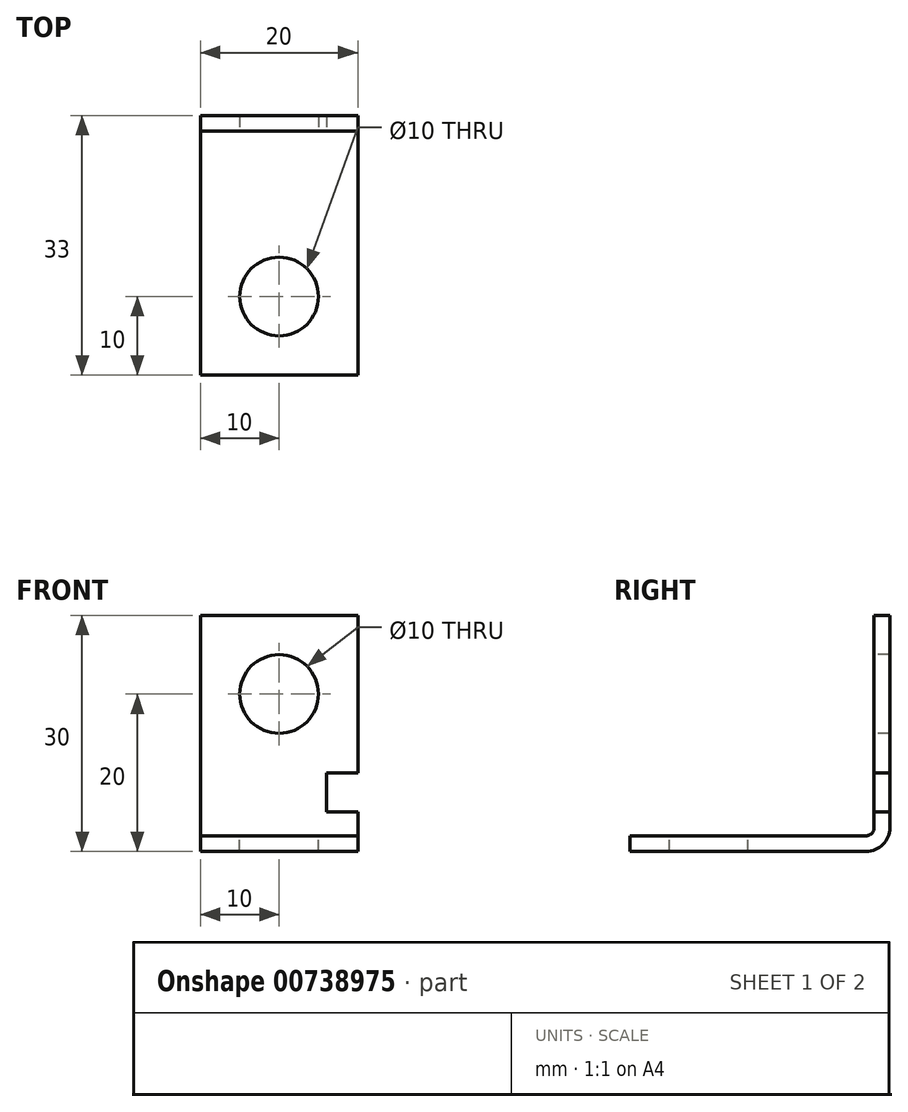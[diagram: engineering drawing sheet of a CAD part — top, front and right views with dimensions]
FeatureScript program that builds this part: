
annotation { "Feature Type Name" : "Feature", "Feature Type Description" : "" }
export const myFeature = defineFeature(function(context is Context, id is Id, definition is map)
    precondition{}
    {
        {
            var Q0;
            Q0=qCreatedBy(makeId("Right.planeOp"),FACE);
            var sketch = newSketch(context, id + "F0", { "sketchPlane" : qUnion([Q0])});
            skLineSegment(sketch, "E0", {"start": v(0, 0) * mm, "end": v(30, 0) * mm});
            skArc(sketch, "E1", {"start": v(30, 0) * mm, "mid": v(32.12, 0.88) * mm, "end": v(33, 3) * mm});
            skLineSegment(sketch, "E2", {"start": v(33, 3) * mm, "end": v(33, 30) * mm});
            skLineSegment(sketch, "E3", {"start": v(33, 30) * mm, "end": v(31, 30) * mm});
            skLineSegment(sketch, "E4", {"start": v(31, 30) * mm, "end": v(31, 3) * mm});
            skLineSegment(sketch, "E5", {"start": v(0, 0) * mm, "end": v(0, 2) * mm});
            skLineSegment(sketch, "E6", {"start": v(0, 2) * mm, "end": v(30, 2) * mm});
            skArc(sketch, "E7", {"start": v(30, 2) * mm, "mid": v(30.7, 2.3) * mm, "end": v(31, 3) * mm});
            skSolve(sketch);
        }
        {
            var Q0;
            Q0 = qSketchRegion(id + "F0", true);
            extrude(context, id + "F1", {"entities" : qUnion([Q0]), "depth" : 20 * mm, "offsetDistance" : 25 * mm});
        }
        {
            var Q0;
            Q0=makeQuery(id+"F1.opExtrude","SWEPT_FACE",FACE,{"disambiguationData":[OSD([sQuery(id+"F0.wireOp",EDGE,"E4")])]});
            var sketch = newSketch(context, id + "F2", { "sketchPlane" : qUnion([Q0])});
            skCircle(sketch, "E8", {"center": v(10, 20) * mm, "radius": 5 * mm});
            skLineSegment(sketch, "E9", {"start": v(20, 10) * mm, "end": v(16, 10) * mm});
            skLineSegment(sketch, "E10", {"start": v(16, 10) * mm, "end": v(16, 5) * mm});
            skLineSegment(sketch, "E11", {"start": v(16, 5) * mm, "end": v(20, 5) * mm});
            skLineSegment(sketch, "E12", {"start": v(20, 5) * mm, "end": v(20, 10) * mm});
            skSolve(sketch);
        }
        {
            var Q0;
            Q0 = qSketchRegion(id + "F2", true);
            extrude(context, id + "F3", {"entities" : qUnion([Q0]), "operationType" : NewBodyOperationType.REMOVE, "oppositeDirection" : true, "depth" : 25 * mm, "offsetDistance" : 25 * mm});
        }
        {
            var Q0;
            Q0=makeQuery(id+"F1.opExtrude","SWEPT_FACE",FACE,{"disambiguationData":[OSD([sQuery(id+"F0.wireOp",EDGE,"E6")])]});
            var sketch = newSketch(context, id + "F4", { "sketchPlane" : qUnion([Q0])});
            skCircle(sketch, "E13", {"center": v(10, 10) * mm, "radius": 5 * mm});
            skSolve(sketch);
        }
        {
            var Q0;
            Q0 = qSketchRegion(id + "F4", true);
            extrude(context, id + "F5", {"entities" : qUnion([Q0]), "operationType" : NewBodyOperationType.REMOVE, "oppositeDirection" : true, "depth" : 25 * mm, "offsetDistance" : 25 * mm});
        }
    });
